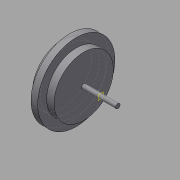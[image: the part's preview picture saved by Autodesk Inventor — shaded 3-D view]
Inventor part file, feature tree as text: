
AUTODESK INVENTOR PART (.ipt)
format: ipt  version: 2015 (Build 190159000, 159)  size: 103,936 bytes
history: native  units: in
note: dims shown in document units (in); Inventor stores cm internally (conversion verified against a paired STEP export)
features: other x3, sketch x3, plane x1
ambient origin geometry x8: Origin, YZ Plane, XZ Plane, XY Plane, X Axis, Y Axis, Z Axis, Center Point
bodies: Solid1 (feature_tree)
feature tree (7):
  other  "rueda.ipt"
  other  "Solid1::rueda.ipt"
  other  "TaggingFeature1"
  sketch  "Sketch2"  dims[d0=0.3937in]
  sketch  "Sketch3"
  sketch  "Sketch7"
  plane  "Work Plane1"
